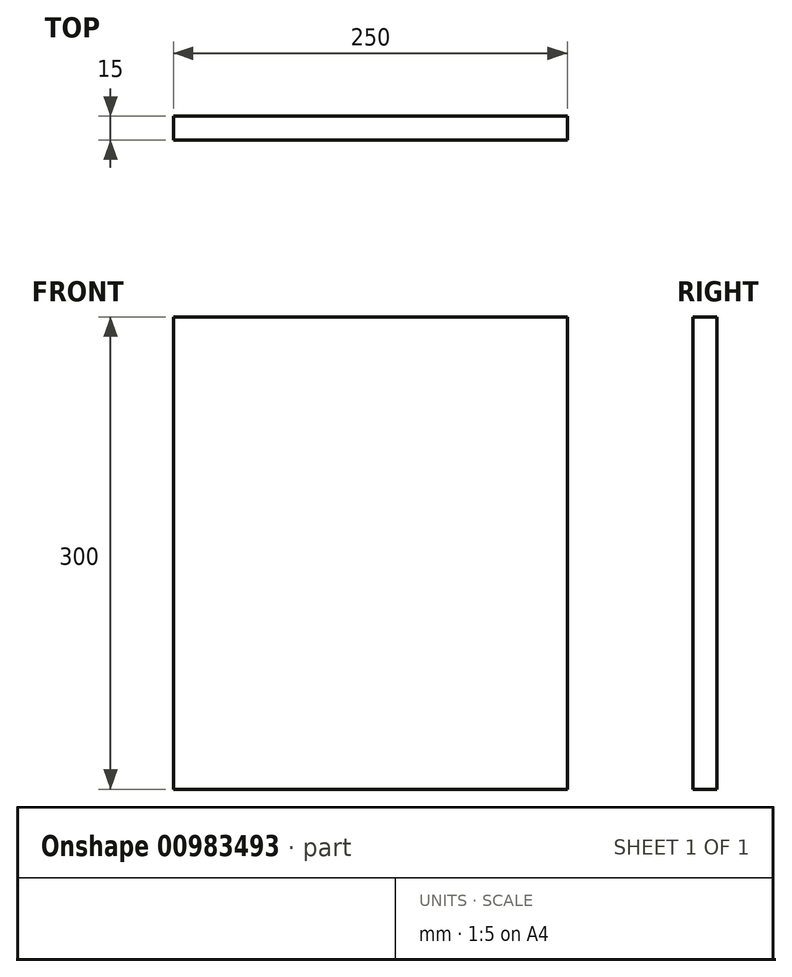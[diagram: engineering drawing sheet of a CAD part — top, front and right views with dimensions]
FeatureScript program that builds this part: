
annotation { "Feature Type Name" : "Feature", "Feature Type Description" : "" }
export const myFeature = defineFeature(function(context is Context, id is Id, definition is map)
    precondition{}
    {
        {
            var Q0;
            Q0=qCreatedBy(makeId("Front.planeOp"),FACE);
            var sketch = newSketch(context, id + "F0", { "sketchPlane" : qUnion([Q0])});
            skLineSegment(sketch, "E0.bottom", {"start": v(0, 0) * mm, "end": v(250, 0) * mm});
            skLineSegment(sketch, "E0.top", {"start": v(0, 300) * mm, "end": v(250, 300) * mm});
            skLineSegment(sketch, "E0.left", {"start": v(0, 0) * mm, "end": v(0, 300) * mm});
            skLineSegment(sketch, "E0.right", {"start": v(250, 0) * mm, "end": v(250, 300) * mm});
            skSolve(sketch);
        }
        {
            var Q0;
            Q0 = qSketchRegion(id + "F0", true);
            extrude(context, id + "F1", {"entities" : qUnion([Q0]), "depth" : 15 * mm, "offsetDistance" : 25 * mm});
        }
    });
